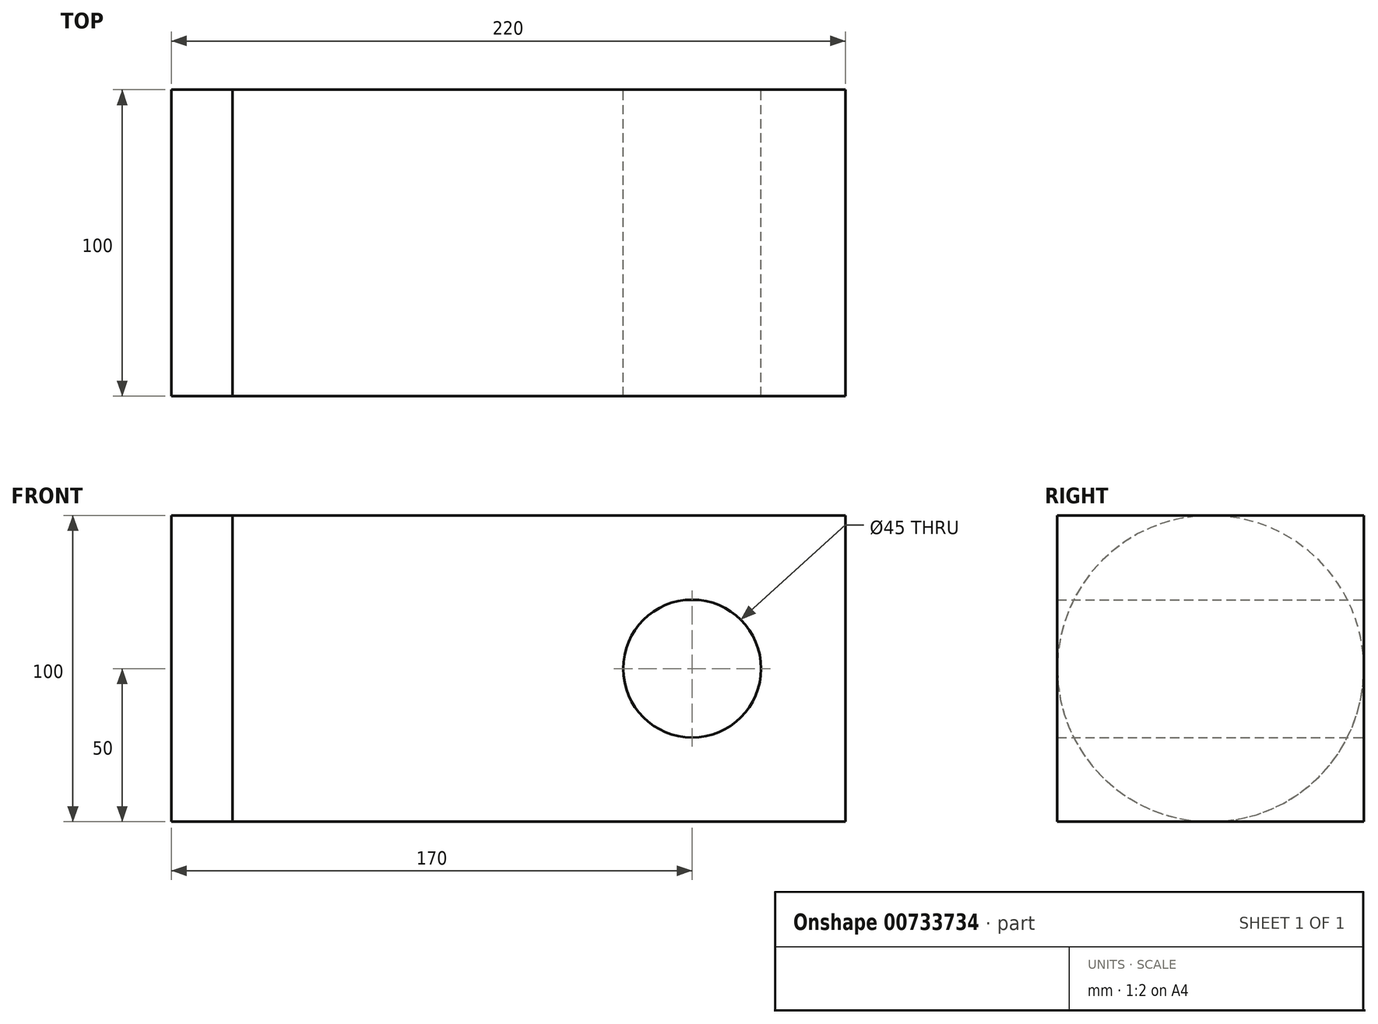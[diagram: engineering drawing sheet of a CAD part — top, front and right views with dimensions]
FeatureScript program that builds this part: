
annotation { "Feature Type Name" : "Feature", "Feature Type Description" : "" }
export const myFeature = defineFeature(function(context is Context, id is Id, definition is map)
    precondition{}
    {
        {
            var Q0;
            Q0=qCreatedBy(makeId("Front.planeOp"),FACE);
            var sketch = newSketch(context, id + "F0", { "sketchPlane" : qUnion([Q0])});
            skLineSegment(sketch, "E0.bottom", {"start": v(100, -50) * mm, "end": v(-100, -50) * mm});
            skLineSegment(sketch, "E0.top", {"start": v(100, 50) * mm, "end": v(-100, 50) * mm});
            skLineSegment(sketch, "E0.left", {"start": v(100, -50) * mm, "end": v(100, 50) * mm});
            skLineSegment(sketch, "E0.right", {"start": v(-100, -50) * mm, "end": v(-100, 50) * mm});
            skPoint(sketch, "E0.middle", {"position": v(0, 0) * mm});
            skLineSegment(sketch, "E1.right", {"start": v(-1000, 0) * mm, "end": v(-1000, 10) * mm});
            skLineSegment(sketch, "E2", {"start": v(100, 0) * mm, "end": v(50, 0) * mm});
            skCircle(sketch, "E3", {"center": v(50, 0) * mm, "radius": 22.5 * mm});
            skSolve(sketch);
        }
        {
            var Q0;
            Q0=makeQuery(id+"F0.imprint","IMPRINT",FACE,{"disambiguationData":[TD([[makeQuery(id+"F0.imprint","IMPRINT",EDGE,{"derivedFrom":sQuery(id+"F0.wireOp",EDGE,"E0.bottom")}),-1.0]])]});
            extrude(context, id + "F1", {"entities" : qUnion([Q0]), "depth" : 100 * mm, "offsetDistance" : 25 * mm});
        }
        {
            var Q0;
            Q0=makeQuery(id+"F1.opExtrude","SWEPT_FACE",FACE,{"disambiguationData":[OSD([sQuery(id+"F0.wireOp",EDGE,"E0.right")])]});
            var sketch = newSketch(context, id + "F2", { "sketchPlane" : qUnion([Q0])});
            skLineSegment(sketch, "E4", {"start": v(100, 0) * mm, "end": v(50, 0) * mm});
            skCircle(sketch, "E5", {"center": v(50, 0) * mm, "radius": 50 * mm});
            skSolve(sketch);
        }
        {
            var Q0;
            Q0=qSketchRegion(id+"F2",true);
            extrude(context, id + "F3", {"entities" : qUnion([Q0]), "operationType" : NewBodyOperationType.ADD, "depth" : 20 * mm, "offsetDistance" : 25 * mm});
        }
    });
